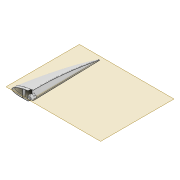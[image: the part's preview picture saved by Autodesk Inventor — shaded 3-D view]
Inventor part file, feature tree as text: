
AUTODESK INVENTOR PART (.ipt)
format: ipt  version: 2022 (Build 260153000, 153)  size: 635,392 bytes
history: native  units: mm
features: sketch x9, extrude x8, plane x4, projected_geometry x2, loft x1, shell x1, fillet x1
ambient origin geometry x8: Origin, YZ Plane, XZ Plane, XY Plane, X Axis, Y Axis, Z Axis, Center Point
bodies: Body1 (feature_tree)
feature tree (26):
  plane  "Work Plane7"
  sketch  "Sketch3"  dims[d45=-250.0mm d46=70.0mm d47=1.0mm d48=5.0mm]
  plane  "Work Plane6"
  sketch  "Sketch17"  dims[d68=0.0mm d69=90.0deg d70=0.0mm d71=90.0deg]
  sketch  "Sketch18"  dims[d72=0.0mm d73=90.0deg d74=0.0mm d75=90.0deg]
  plane  "Work Plane8"
  loft  "Loft4"
  shell  "Shell3"  Thickness=5.0mm
  plane  "Work Plane10"
  sketch  "Sketch32"  dims[d104=66.0mm d122=0.5mm d123=0.0mm]
  extrude  "Extrusion19"  TaperAngle=0.0deg  [1 undecoded]
  extrude  "Extrusion20"  TaperAngle=0.0deg  [1 undecoded]
  sketch  "Sketch36"  dims[d124=0.5mm d125=0.0mm d135=9.8mm]
  extrude  "Extrusion24"  Depth=1.0mm
  extrude  "Extrusion25"  Depth=0.5mm TaperAngle=0.0deg
  extrude  "Extrusion26"  Depth=9.8mm
  extrude  "Extrusion27"  Depth=12.2mm
  extrude  "Extrusion28"  Depth=1.0mm TaperAngle=0.0deg
  fillet  "Fillet4"  Radius=1.5mm
  extrude  "Extrusion31"  Depth=10.0mm TaperAngle=0.0deg
  sketch  "Sketch19"  dims[d76=0.0mm d77=90.0deg d78=1.0mm]
  sketch  "Sketch37"  dims[d136=4.15mm d137=12.2mm]
  sketch  "Sketch38"  dims[d138=2.0mm d139=1.0mm d140=0.0mm d141=1.5mm]
  sketch  "Sketch41"  dims[d142=12.0mm d143=0.0mm d144=10.0mm d145=0.0mm d146=2.1mm d147=6.0mm d148=100.0mm d149=0.0mm d152=8.0mm d153=0.0mm d154=5.0mm d158=2.3mm d159=5.3mm d160=1.15mm d170=3.0mm d171=3.0mm d172=40.0mm d173=1.0mm d174=4.0mm d175=10.0mm d176=0.0mm]
  projected_geometry  "Projected Loop14"
  projected_geometry  "Project Cut Edges5"
note: 2 required parameter values undecoded (feature->parameter linkage not recoverable at this tier; creation-order binding heuristic only, values carry confidence <= 0.55)
